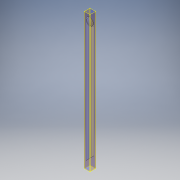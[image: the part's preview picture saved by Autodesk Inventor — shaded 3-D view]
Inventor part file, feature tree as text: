
AUTODESK INVENTOR PART (.ipt)
format: ipt  version: 2018 (Build 220112000, 112)  size: 100,864 bytes
history: native  units: mm
features: other x7, extrude x1, sketch x1
ambient origin geometry x8: Origin, YZ Plane, XZ Plane, XY Plane, X Axis, Y Axis, Z Axis, Center Point
bodies: Body1 (feature_tree)
feature tree (9):
  other  "ソリッド1"
  extrude  "押し出し1"  Depth=27.2mm
  other  "面の勾配1"
  other  "面の勾配2"
  other  "作業平面1"
  other  "作業平面2"
  other  "作業平面3"
  other  "作業平面4"
  sketch  "スケッチ1"
